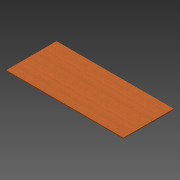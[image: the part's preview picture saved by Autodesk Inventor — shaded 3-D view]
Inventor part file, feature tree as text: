
AUTODESK INVENTOR PART (.ipt)
format: ipt  version: 2013 (Build 170138000, 138)  size: 76,288 bytes
history: native  units: in
note: dims shown in document units (in); Inventor stores cm internally (conversion verified against a paired STEP export)
features: extrude x1, sketch x1
ambient origin geometry x8: Origin, YZ Plane, XZ Plane, XY Plane, X Axis, Y Axis, Z Axis, Center Point
bodies: Solid1 (feature_tree)
feature tree (2):
  extrude  "Extrusion1"  Depth=24.0in
  sketch  "Sketch1"  dims[d0=58.0in d1=24.0in d2=0.5in d3=0.0in]
